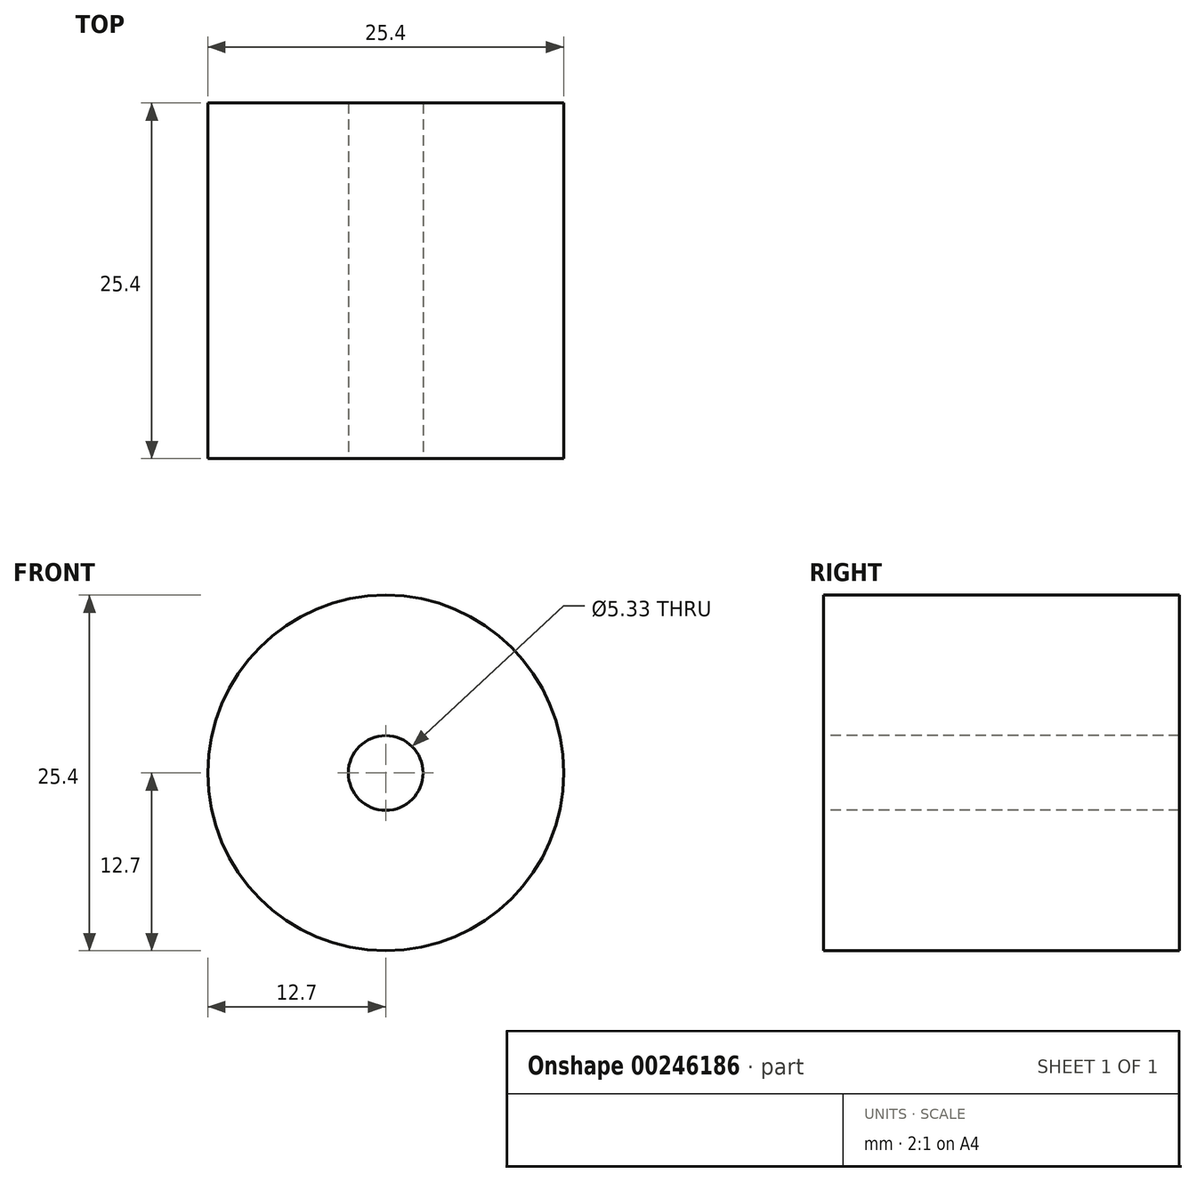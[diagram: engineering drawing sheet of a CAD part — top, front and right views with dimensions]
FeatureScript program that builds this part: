
annotation { "Feature Type Name" : "Feature", "Feature Type Description" : "" }
export const myFeature = defineFeature(function(context is Context, id is Id, definition is map)
    precondition{}
    {
        {
            var Q0;
            Q0=qCreatedBy(makeId("Front.planeOp"),FACE);
            var sketch = newSketch(context, id + "F0", { "sketchPlane" : qUnion([Q0])});
            skCircle(sketch, "E0", {"center": v(0, 0) * mm, "radius": 12.7 * mm});
            skSolve(sketch);
        }
        {
            var Q0;
            Q0=makeQuery(id+"F0.imprint","IMPRINT",FACE,{"disambiguationData":[TD([[makeQuery(id+"F0.imprint","IMPRINT",EDGE,{"derivedFrom":sQuery(id+"F0.wireOp",EDGE,"E0")}),1.0]])]});
            extrude(context, id + "F1", {"entities" : qUnion([Q0]), "depth" : 25.4 * mm});
        }
        {
            var Q0;
            Q0=sQuery(id+"F0.wireOp",VERTEX,"E0.center");
            var Q1;
            Q1=makeQuery(id+"F1.opExtrude","SWEPT_BODY",BODY,{"disambiguationData":[OSD([sQuery(id+"F0.wireOp",EDGE,"E0")])]});
            hole(context, id + "F2", {"style" : HoleStyle.SIMPLE, "endStyle" : HoleEndStyle.THROUGH, "oppositeDirection" : true, "holeDiameter" : 5.33 * mm, "tappedDepth" : 12.7 * mm, "tapClearance" : 3, "locations" : qUnion([Q0]), "scope" : qUnion([Q1])});
        }
    });
